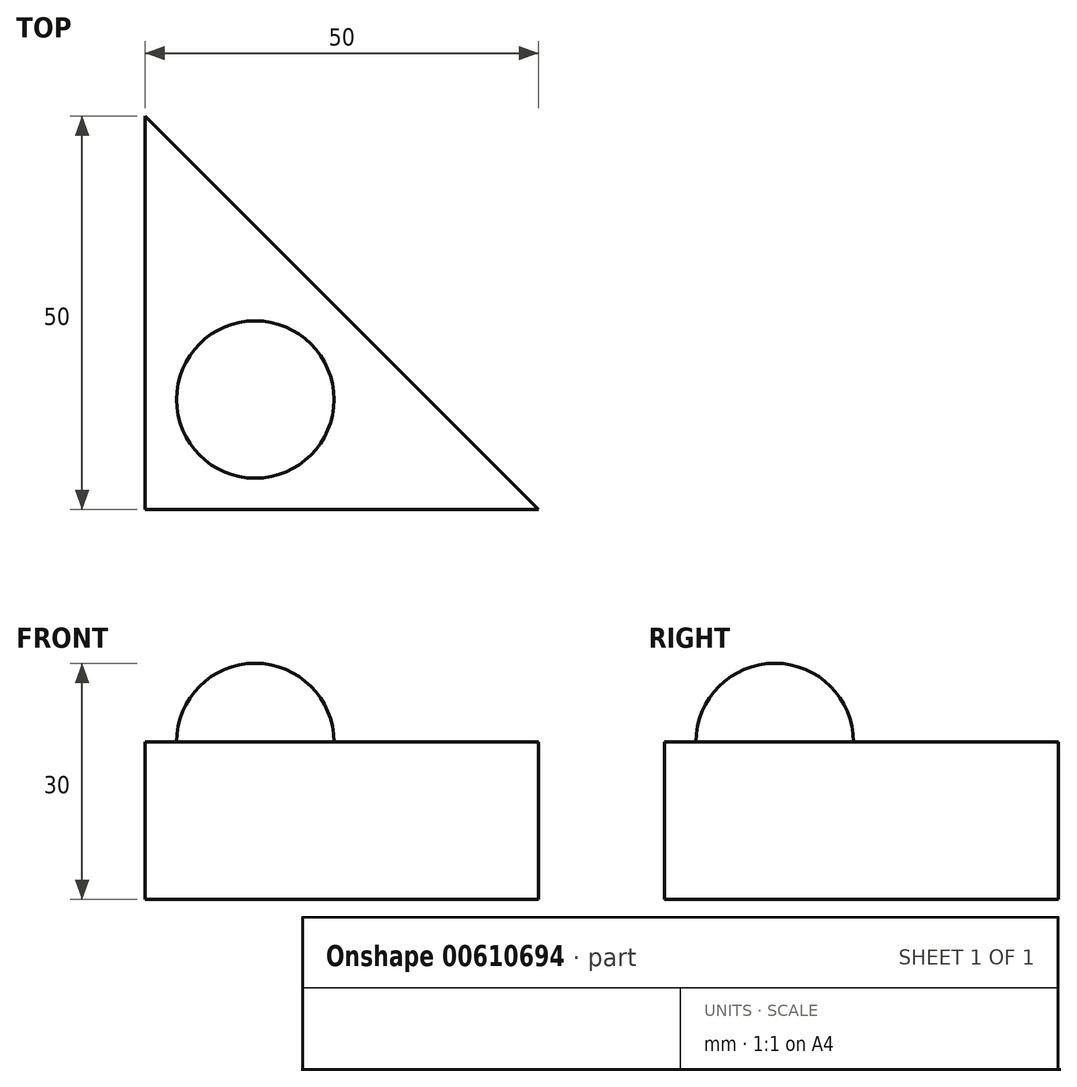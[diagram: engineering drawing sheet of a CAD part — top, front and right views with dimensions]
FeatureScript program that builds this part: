
annotation { "Feature Type Name" : "Feature", "Feature Type Description" : "" }
export const myFeature = defineFeature(function(context is Context, id is Id, definition is map)
    precondition{}
    {
        {
            var Q0;
            Q0=qCreatedBy(makeId("Top.planeOp"),FACE);
            var sketch = newSketch(context, id + "F0", { "sketchPlane" : qUnion([Q0])});
            skLineSegment(sketch, "E0", {"start": v(0, 0) * mm, "end": v(50, 0) * mm});
            skLineSegment(sketch, "E1", {"start": v(50, 0) * mm, "end": v(0, 50) * mm});
            skLineSegment(sketch, "E2", {"start": v(0, 50) * mm, "end": v(0, 0) * mm});
            skSolve(sketch);
        }
        {
            var Q0;
            Q0=makeQuery(id+"F0.imprint","IMPRINT",FACE,{"disambiguationData":[TD([[makeQuery(id+"F0.imprint","IMPRINT",EDGE,{"derivedFrom":sQuery(id+"F0.wireOp",EDGE,"E0")}),1.0]])]});
            extrude(context, id + "F1", {"entities" : qUnion([Q0]), "depth" : 20 * mm, "offsetDistance" : 25 * mm});
        }
        {
            var Q0;
            Q0=makeQuery(id+"F1.opExtrude","CAP_FACE",FACE,{"disambiguationData":[OSD([sQuery(id+"F0.wireOp",EDGE,"E0"),sQuery(id+"F0.wireOp",EDGE,"E1"),sQuery(id+"F0.wireOp",EDGE,"E2")])],"isStart":false});
            var sketch = newSketch(context, id + "F2", { "sketchPlane" : qUnion([Q0])});
            skArc(sketch, "E3", {"start": v(14, 24) * mm, "mid": v(4, 14) * mm, "end": v(14, 4) * mm});
            skLineSegment(sketch, "E4", {"start": v(14, 4) * mm, "end": v(14, 24) * mm});
            skSolve(sketch);
        }
        {
            var Q0;
            Q0=makeQuery(id+"F2.imprint","IMPRINT",FACE,{"disambiguationData":[TD([[makeQuery(id+"F2.imprint","IMPRINT",EDGE,{"derivedFrom":sQuery(id+"F2.wireOp",EDGE,"E3")}),1.0]])]});
            var Q1;
            Q1=sQuery(id+"F2.wireOp",EDGE,"E4");
            revolve(context, id + "F3", {"operationType" : NewBodyOperationType.ADD, "entities" : qUnion([Q0]), "axis" : qUnion([Q1]), "revolveType" : RevolveType.FULL});
        }
    });
